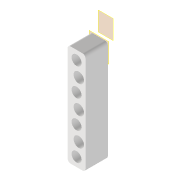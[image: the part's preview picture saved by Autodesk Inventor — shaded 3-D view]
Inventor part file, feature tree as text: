
AUTODESK INVENTOR PART (.ipt)
format: ipt  version: 2022 (Build 260153000, 153)  size: 173,056 bytes
history: native  units: mm
features: reference x12, other x6, sketch x3, plane x2, extrude x2, hole x1, fillet x1, projected_geometry x1
ambient origin geometry x8: Origin, YZ Plane, XZ Plane, XY Plane, X Axis, Y Axis, Z Axis, Center Point
bodies: Volumenkörper1 (feature_tree)
feature tree (28):
  plane  "Arbeitsebene1"
  plane  "Arbeitsebene2"
  extrude  "Extrusion1"  Depth=7.2mm
  extrude  "Extrusion2"  Depth=7.2mm
  hole  "Bohrung1"  [1 undecoded]
  fillet  "Rundung1"  Radius=3.2mm
  sketch  "Skizze2"  dims[d0=7.3mm d1=7.2mm]
  reference  "Referenz1"
  reference  "Referenz2"
  reference  "Referenz3"
  reference  "Referenz4"
  reference  "Referenz5"
  reference  "Referenz6"
  reference  "Referenz7"
  reference  "Referenz8"
  reference  "Referenz9"
  reference  "Referenz10"
  reference  "Referenz11"
  reference  "Referenz12"
  sketch  "Skizze3"  dims[d2=7.2mm d3=7.2mm]
  projected_geometry  "Projizierte Kontur1"
  sketch  "Skizze4"  dims[d4=3.2mm d5=3.2mm d6=3.2mm d7=3.2mm d8=3.2mm d9=7.0mm d10=10.0mm d11=0.0mm d12=6.7mm d13=6.7mm d14=6.7mm d15=6.7mm d16=5.0mm d17=0.0mm d18=3.2mm d19=6.0mm d20=7.0mm d21=10.0mm d22=90.0deg d23=8.0mm d24=20.594885mm d25=2.0mm]
  other  "Omnicscope_Xiao.iam"
  other  "00_Seeeduino Xiao:1"
  other  "00_Seeeduino Xiao:7"
  other  "00_Seeeduino Xiao:13"
  other  "Omniscope_USBC_Bar:1"
  other  "00_Seeeduino Xiao:19"
note: 1 required parameter value undecoded (feature->parameter linkage not recoverable at this tier; creation-order binding heuristic only, values carry confidence <= 0.55)
